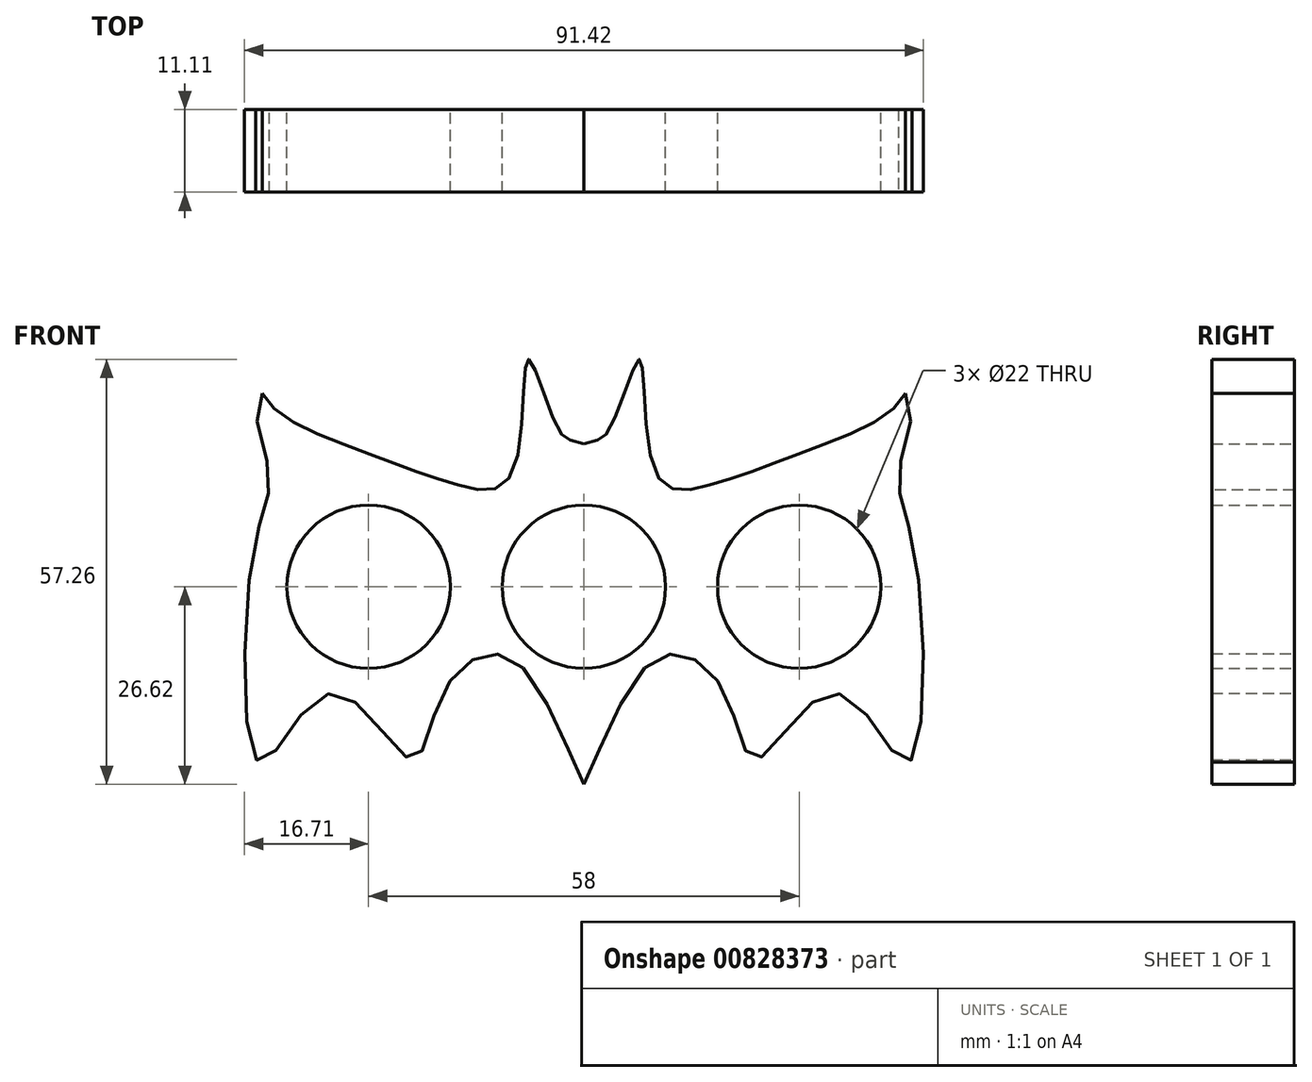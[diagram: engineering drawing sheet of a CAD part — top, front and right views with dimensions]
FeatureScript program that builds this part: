
annotation { "Feature Type Name" : "Feature", "Feature Type Description" : "" }
export const myFeature = defineFeature(function(context is Context, id is Id, definition is map)
    precondition{}
    {
        {
            var Q0;
            Q0=qCreatedBy(makeId("Front.planeOp"),FACE);
            var sketch = newSketch(context, id + "F0", { "sketchPlane" : qUnion([Q0])});
            skFitSpline(sketch, "E0", {"points": [v(-24.73, 14.9) * mm, v(-17.25, 10.5) * mm, v(-9.65, 7.82) * mm, v(-5.58, 8.63) * mm, v(-4.3, 17.5) * mm, v(-1.9, 12) * mm, v(0, 11) * mm], "startDerivative": vector(12.18, -28.87) * mm, "endDerivative": vector(30.73, -10.5) * mm});
            skFitSpline(sketch, "E1", {"points": [v(-24.73, 14.9) * mm, v(-24.26, 9.07) * mm, v(-25.4, 2.9) * mm, v(-24.97, -13.49) * mm, v(-20.81, -8.83) * mm, v(-17.16, -9.24) * mm, v(-13.1, -13.3) * mm, v(-11.07, -8.63) * mm, v(-7.75, -5.26) * mm, v(-4.37, -6.58) * mm, v(0, -15.2) * mm], "startDerivative": vector(-40.25, -24.7) * mm, "endDerivative": vector(21.53, -40.83) * mm});
            skLineSegment(sketch, "E2", {"start": v(0, 11) * mm, "end": v(0, -15.2) * mm});
            skFitSpline(sketch, "E3.MirrorCS", {"points": [v(24.73, 14.9) * mm, v(24.26, 9.07) * mm, v(25.4, 2.9) * mm, v(24.97, -13.49) * mm, v(20.81, -8.83) * mm, v(17.16, -9.24) * mm, v(13.1, -13.3) * mm, v(11.07, -8.63) * mm, v(7.75, -5.26) * mm, v(4.37, -6.58) * mm, v(0, -15.2) * mm], "startDerivative": vector(40.25, -24.7) * mm, "endDerivative": vector(-21.53, -40.83) * mm});
            skFitSpline(sketch, "E4.MirrorCS", {"points": [v(24.73, 14.9) * mm, v(17.25, 10.5) * mm, v(9.65, 7.82) * mm, v(5.58, 8.63) * mm, v(4.3, 17.5) * mm, v(1.9, 12) * mm, v(0, 11) * mm], "startDerivative": vector(-12.18, -28.87) * mm, "endDerivative": vector(-30.73, -10.5) * mm});
            skSolve(sketch);
        }
        {
            var Q0;
            Q0 = qSketchRegion(id + "F0", true);
            extrude(context, id + "F1", {"entities" : qUnion([Q0]), "depth" : 6.35 * mm, "offsetDistance" : 25.4 * mm});
        }
        {
            var Q0;
            Q0=qCreatedBy(makeId("Front.planeOp"),FACE);
            var sketch = newSketch(context, id + "F2", { "sketchPlane" : qUnion([Q0])});
            skCircle(sketch, "E5", {"center": v(0, 0) * mm, "radius": 11 * mm});
            skCircle(sketch, "E6", {"center": v(-29, 0) * mm, "radius": 11 * mm});
            skCircle(sketch, "E7.MirrorC", {"center": v(29, 0) * mm, "radius": 11 * mm});
            skSolve(sketch);
        }
        {
            var Q0;
            Q0=makeQuery(id+"F1.opExtrude","SWEPT_BODY",BODY,{"disambiguationData":[OSD([sQuery(id+"F0.wireOp",EDGE,"E0"),sQuery(id+"F0.wireOp",EDGE,"E1"),sQuery(id+"F0.wireOp",EDGE,"E3.MirrorCS"),sQuery(id+"F0.wireOp",EDGE,"E4.MirrorCS")])]});
            var Q1;
            Q1=sQuery(id+"F2.wireOp",VERTEX,"E5.center");
            transform(context, id + "F3", {"entities" : qUnion([Q0]), "transformType" : TransformType.SCALE_UNIFORMLY, "scale" : 1.75, "scalePoint" : qUnion([Q1]), "makeCopy" : false});
        }
        {
            var Q0;
            Q0 = qSketchRegion(id + "F2", true);
            extrude(context, id + "F4", {"entities" : qUnion([Q0]), "operationType" : NewBodyOperationType.REMOVE, "endBound" : BoundingType.THROUGH_ALL, "depth" : 25.4 * mm, "offsetDistance" : 25.4 * mm});
        }
    });
